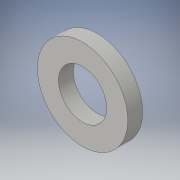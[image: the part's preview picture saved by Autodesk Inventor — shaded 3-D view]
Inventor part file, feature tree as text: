
AUTODESK INVENTOR PART (.ipt)
format: ipt  version: 2016 (Build 200138000, 138)  size: 111,616 bytes
history: native  units: in
note: dims shown in document units (in); Inventor stores cm internally (conversion verified against a paired STEP export)
features: extrude x1, sketch x1
ambient origin geometry x8: Origin, YZ Plane, XZ Plane, XY Plane, X Axis, Y Axis, Z Axis, Center Point
bodies: Solid1 (feature_tree)
feature tree (2):
  extrude  "Extrusion1"  Depth=0.0394in
  sketch  "Sketch1"  dims[d0=0.24in d1=0.128in d2=0.0394in d3=0.0in]
